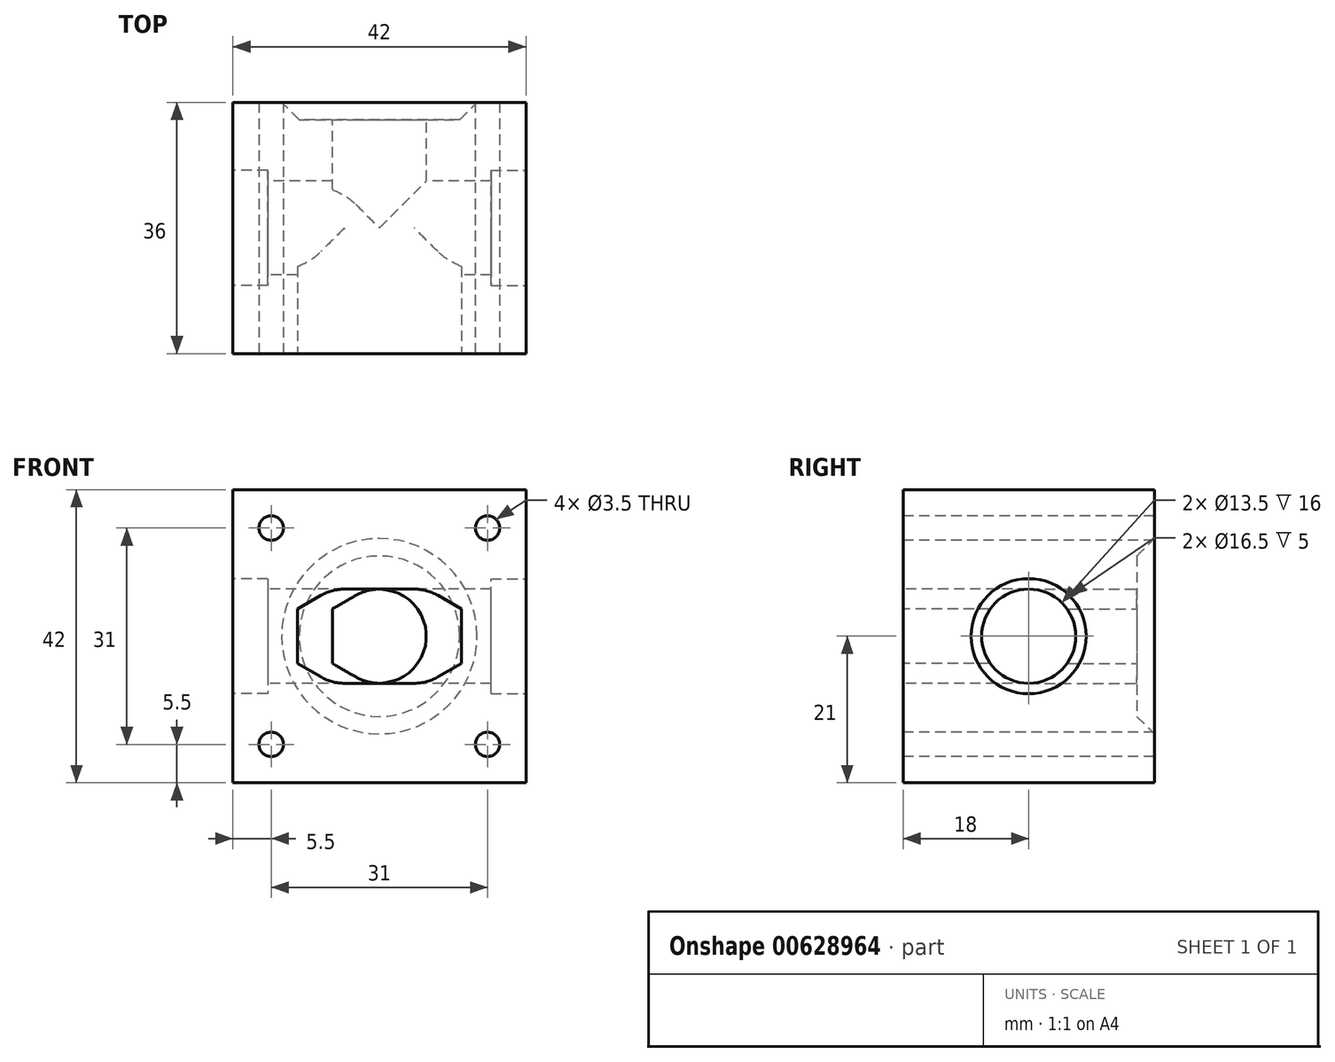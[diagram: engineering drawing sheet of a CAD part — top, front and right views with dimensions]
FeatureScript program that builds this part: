
annotation { "Feature Type Name" : "Feature", "Feature Type Description" : "" }
export const myFeature = defineFeature(function(context is Context, id is Id, definition is map)
    precondition{}
    {
        {
            var Q0;
            Q0=qCreatedBy(makeId("Front.planeOp"),FACE);
            var sketch = newSketch(context, id + "F0", { "sketchPlane" : qUnion([Q0])});
            skLineSegment(sketch, "E0.bottom", {"start": v(-21, 21) * mm, "end": v(21, 21) * mm});
            skLineSegment(sketch, "E0.top", {"start": v(-21, -21) * mm, "end": v(21, -21) * mm});
            skLineSegment(sketch, "E0.left", {"start": v(-21, 21) * mm, "end": v(-21, -21) * mm});
            skLineSegment(sketch, "E0.right", {"start": v(21, 21) * mm, "end": v(21, -21) * mm});
            skPoint(sketch, "E0.middle", {"position": v(0, 0) * mm});
            skSolve(sketch);
        }
        {
            var Q0;
            Q0 = qSketchRegion(id + "F0", true);
            extrude(context, id + "F1", {"entities" : qUnion([Q0]), "endBound" : BoundingType.SYMMETRIC, "depth" : 36 * mm, "offsetDistance" : 25 * mm});
        }
        {
            var Q0;
            Q0=makeQuery(id+"F1.opExtrude","CAP_FACE",FACE,{"disambiguationData":[OSD([sQuery(id+"F0.wireOp",EDGE,"E0.bottom"),sQuery(id+"F0.wireOp",EDGE,"E0.top"),sQuery(id+"F0.wireOp",EDGE,"E0.left"),sQuery(id+"F0.wireOp",EDGE,"E0.right")])],"isStart":false});
            var sketch = newSketch(context, id + "F2", { "sketchPlane" : qUnion([Q0])});
            skCircle(sketch, "E1", {"center": v(-15.5, 15.5) * mm, "radius": 1.75 * mm});
            skCircle(sketch, "E2.1.0", {"center": v(-15.5, -15.5) * mm, "radius": 1.75 * mm});
            skCircle(sketch, "E2.2.0", {"center": v(15.5, -15.5) * mm, "radius": 1.75 * mm});
            skCircle(sketch, "E2.3.0", {"center": v(15.5, 15.5) * mm, "radius": 1.75 * mm});
            skPoint(sketch, "E2.center", {"position": v(0, 0) * mm});
            skSolve(sketch);
        }
        {
            var Q0;
            Q0 = qSketchRegion(id + "F2", true);
            extrude(context, id + "F3", {"entities" : qUnion([Q0]), "operationType" : NewBodyOperationType.REMOVE, "endBound" : BoundingType.THROUGH_ALL, "oppositeDirection" : true, "depth" : 25 * mm, "offsetDistance" : 25 * mm});
        }
        {
            var Q0;
            Q0=makeQuery(id+"F1.opExtrude","SWEPT_FACE",FACE,{"disambiguationData":[OSD([sQuery(id+"F0.wireOp",EDGE,"E0.left")])]});
            var sketch = newSketch(context, id + "F4", { "sketchPlane" : qUnion([Q0])});
            skCircle(sketch, "E3", {"center": v(0, 0) * mm, "radius": 6.75 * mm});
            skSolve(sketch);
        }
        {
            var Q0;
            Q0 = qSketchRegion(id + "F4", true);
            extrude(context, id + "F5", {"entities" : qUnion([Q0]), "operationType" : NewBodyOperationType.REMOVE, "endBound" : BoundingType.THROUGH_ALL, "oppositeDirection" : true, "depth" : 25 * mm, "offsetDistance" : 25 * mm});
        }
        {
            var Q0;
            Q0=makeQuery(id+"F1.opExtrude","SWEPT_FACE",FACE,{"disambiguationData":[OSD([sQuery(id+"F0.wireOp",EDGE,"E0.left")])]});
            var sketch = newSketch(context, id + "F6", { "sketchPlane" : qUnion([Q0])});
            skCircle(sketch, "E4", {"center": v(0, 0) * mm, "radius": 8.25 * mm});
            skSolve(sketch);
        }
        {
            var Q0;
            Q0 = qSketchRegion(id + "F6", true);
            extrude(context, id + "F7", {"entities" : qUnion([Q0]), "operationType" : NewBodyOperationType.REMOVE, "oppositeDirection" : true, "depth" : 5 * mm, "offsetDistance" : 25 * mm});
        }
        {
            var Q0;
            Q0=makeQuery(id+"F1.opExtrude","SWEPT_FACE",FACE,{"disambiguationData":[OSD([sQuery(id+"F0.wireOp",EDGE,"E0.right")])]});
            var sketch = newSketch(context, id + "F8", { "sketchPlane" : qUnion([Q0])});
            skCircle(sketch, "E5", {"center": v(0, 0) * mm, "radius": 8.25 * mm});
            skSolve(sketch);
        }
        {
            var Q0;
            Q0 = qSketchRegion(id + "F8", true);
            extrude(context, id + "F9", {"entities" : qUnion([Q0]), "operationType" : NewBodyOperationType.REMOVE, "oppositeDirection" : true, "depth" : 5 * mm, "offsetDistance" : 25 * mm});
        }
        {
            var Q0;
            Q0=makeQuery(id+"F1.opExtrude","CAP_FACE",FACE,{"disambiguationData":[OSD([sQuery(id+"F0.wireOp",EDGE,"E0.bottom"),sQuery(id+"F0.wireOp",EDGE,"E0.top"),sQuery(id+"F0.wireOp",EDGE,"E0.left"),sQuery(id+"F0.wireOp",EDGE,"E0.right")])],"isStart":true});
            var sketch = newSketch(context, id + "F10", { "sketchPlane" : qUnion([Q0])});
            skArc(sketch, "E6", {"start": v(3.38, 5.85) * mm, "mid": v(-6.75, 0) * mm, "end": v(3.37, -5.85) * mm});
            skLineSegment(sketch, "E7", {"start": v(3.38, 5.85) * mm, "end": v(6.75, 3.9) * mm});
            skLineSegment(sketch, "E8", {"start": v(6.75, 3.9) * mm, "end": v(6.75, 0) * mm});
            skLineSegment(sketch, "E9.MirrorCS", {"start": v(3.37, -5.85) * mm, "end": v(6.75, -3.9) * mm});
            skLineSegment(sketch, "E10.MirrorCS", {"start": v(6.75, -3.9) * mm, "end": v(6.75, 0) * mm});
            skSolve(sketch);
        }
        {
            var Q0;
            Q0 = qSketchRegion(id + "F10", true);
            extrude(context, id + "F11", {"entities" : qUnion([Q0]), "operationType" : NewBodyOperationType.REMOVE, "endBound" : BoundingType.UP_TO_NEXT, "oppositeDirection" : true, "depth" : 25 * mm, "offsetDistance" : 25 * mm});
        }
        {
            var Q0;
            Q0=makeQuery(id+"F1.opExtrude","CAP_FACE",FACE,{"disambiguationData":[OSD([sQuery(id+"F0.wireOp",EDGE,"E0.bottom"),sQuery(id+"F0.wireOp",EDGE,"E0.top"),sQuery(id+"F0.wireOp",EDGE,"E0.left"),sQuery(id+"F0.wireOp",EDGE,"E0.right")])],"isStart":true});
            var sketch = newSketch(context, id + "F12", { "sketchPlane" : qUnion([Q0])});
            skCircle(sketch, "E11", {"center": v(0, 0) * mm, "radius": 14 * mm});
            skSolve(sketch);
        }
        {
            var Q0;
            Q0 = qSketchRegion(id + "F12", true);
            extrude(context, id + "F13", {"entities" : qUnion([Q0]), "operationType" : NewBodyOperationType.REMOVE, "oppositeDirection" : true, "depth" : 2.5 * mm, "offsetDistance" : 25 * mm});
        }
        {
            var Q0;
            Q0=makeQuery(id+"F13.boolean.opBoolean","COPY",EDGE,{"derivedFrom":makeQuery(id+"F13.opExtrude","CAP_EDGE",EDGE,{"disambiguationData":[OSD([sQuery(id+"F12.wireOp",EDGE,"E11")])],"isStart":false})});
            chamfer(context, id + "F14", {"entities" : qUnion([Q0]), "width" : 2.5 * mm, "tangentPropagation" : true});
        }
        {
            var Q0;
            Q0=makeQuery(id+"F1.opExtrude","CAP_FACE",FACE,{"disambiguationData":[OSD([sQuery(id+"F0.wireOp",EDGE,"E0.bottom"),sQuery(id+"F0.wireOp",EDGE,"E0.top"),sQuery(id+"F0.wireOp",EDGE,"E0.left"),sQuery(id+"F0.wireOp",EDGE,"E0.right")])],"isStart":false});
            var sketch = newSketch(context, id + "F15", { "sketchPlane" : qUnion([Q0])});
            skLineSegment(sketch, "E12", {"start": v(-21, 0) * mm, "end": v(21, 0) * mm, "construction": true});
            skArc(sketch, "E13", {"start": v(-8.37, -5.85) * mm, "mid": v(-6.75, -6.52) * mm, "end": v(-5, -6.75) * mm});
            skLineSegment(sketch, "E14", {"start": v(-8.37, 5.85) * mm, "end": v(-11.75, 3.9) * mm});
            skLineSegment(sketch, "E15", {"start": v(-11.75, 3.9) * mm, "end": v(-11.75, 0) * mm});
            skLineSegment(sketch, "E16.MirrorCS", {"start": v(-8.37, -5.85) * mm, "end": v(-11.75, -3.9) * mm});
            skLineSegment(sketch, "E17.MirrorCS", {"start": v(-11.75, -3.9) * mm, "end": v(-11.75, 0) * mm});
            skLineSegment(sketch, "E18", {"start": v(0, -21) * mm, "end": v(0, 21) * mm, "construction": true});
            skLineSegment(sketch, "E19", {"start": v(-5, 6.75) * mm, "end": v(0, 6.75) * mm});
            skLineSegment(sketch, "E20", {"start": v(-5, -6.75) * mm, "end": v(0, -6.75) * mm});
            skArc(sketch, "E21.trimOffspring", {"start": v(-5, 6.75) * mm, "mid": v(-6.75, 6.52) * mm, "end": v(-8.38, 5.85) * mm});
            skLineSegment(sketch, "E22.MirrorCS", {"start": v(5, -6.75) * mm, "end": v(0, -6.75) * mm});
            skArc(sketch, "E23.MirrorCS", {"start": v(8.37, -5.85) * mm, "mid": v(6.75, -6.52) * mm, "end": v(5, -6.75) * mm});
            skLineSegment(sketch, "E24.MirrorCS", {"start": v(8.37, -5.85) * mm, "end": v(11.75, -3.9) * mm});
            skLineSegment(sketch, "E25.MirrorCS", {"start": v(11.75, -3.9) * mm, "end": v(11.75, 0) * mm});
            skLineSegment(sketch, "E26.MirrorCS", {"start": v(11.75, 3.9) * mm, "end": v(11.75, 0) * mm});
            skLineSegment(sketch, "E27.MirrorCS", {"start": v(5, 6.75) * mm, "end": v(0, 6.75) * mm});
            skLineSegment(sketch, "E28.MirrorCS", {"start": v(8.38, 5.85) * mm, "end": v(11.75, 3.9) * mm});
            skArc(sketch, "E29.MirrorCS", {"start": v(5, 6.75) * mm, "mid": v(6.75, 6.52) * mm, "end": v(8.38, 5.85) * mm});
            skSolve(sketch);
        }
        {
            var Q0;
            Q0 = qSketchRegion(id + "F15", true);
            extrude(context, id + "F16", {"entities" : qUnion([Q0]), "operationType" : NewBodyOperationType.REMOVE, "endBound" : BoundingType.UP_TO_NEXT, "oppositeDirection" : true, "depth" : 25 * mm, "offsetDistance" : 25 * mm});
        }
    });
